# Revit family: RN 55046 Optipress-Therm-Vis de rappel
name_source: partatom
category: Rohrformteile
units: mm (PartAtom-declared; Revit-internal decimal feet)

## family parameters
Arbeitsebenenbasiert = Nein
Beim Laden mit Abzugskörper schneiden = Nein
Bemaßung runder Anschluss = Durchmesser verwenden
Gemeinsam genutzt = Nein
Immer vertikal = Ja
Teiletyp = Verbindung

## types (7) — shared parameters
1.010.00.2 Blattnummer der Richtlinie = 29
1.010.00.3 Ausgabedatum (Monat) der Richtlinie = 201308
1.010.00.4 Herstellername = R. Nussbaum AG
1.010.00.5 Revisionsdatum der Datei = 20190521
1.010.00.6 Webadresse des Herstellers = http://www.nussbaum.ch
1.100.00.4 Produktbezeichnung = Versorgung
1.110.00.2 Index = 1
1.110.00.4 Produktbezeichnung = Optipress-Therm
1.960/3L.00.8 Link (URL) = https://www.nussbaum.ch
29.700.00.4 Produktname = Optipress-Therm-Verschraubung, mit Aussengewinde
29.700.00.5 Produktkennung = 2
29.700.00.6 Querschnittsform = 1
29.700.00.7 Nennweitensystem = DN
29.700.00.8 Nenndrucksystem = PN
29.710.02.4 Nenndruck = 16
29.710.02.5 max. zul. Überdruck [hPa] = 1600
29.710.02.7 max. zul. Dauer-Betriebsdruck [hPa] = 1600
29.710.02.9 max. zul. Dauer-Betriebstemperatur [°C] = 95
Connector Visibility = Nein
EnclosingSpace Visibility = Nein
Hersteller = R. Nussbaum AG

## per-type parameters (varying)
| type | 1.800.00.3 TGA-Nummer | 1.800.00.4 Kommentarfeld | 1.810.00.3 Hersteller-Bestellnummer | 1.810.00.4 DATANORM-Nummer | 1.810.00.5 StLB-Nummer | 1.810.00.6 GTIN-Nummer | 29.710.02.10 Formstück-Gewicht [kg] | 29.710.02.3 Benennung | CONNECTOR0_DIAMETER_dX_0r | CONNECTOR0_dX_01 | CONNECTOR0_ref_dX | CONNECTOR1_DIAMETER_dX_0r | CONNECTOR1_dX_00 | CONNECTOR1_dX_01 | CONNECTOR1_ref_dX | Modell | R. Nussbaum AG 55046.22 de Visibility | R. Nussbaum AG 55046.25 de Visibility | R. Nussbaum AG 55046.26 de Visibility | R. Nussbaum AG 55046.27 de Visibility | R. Nussbaum AG 55046.28 de Visibility | R. Nussbaum AG 55046.29 de Visibility | R. Nussbaum AG 55046.30 de Visibility | Typenkommentare |
| DN=1 | 01900100000000000000000000000000000000000000000026000000000000000007 | 55046.30, Optipress-Therm-Verschraubung, mit Aussengewinde, DN=20, L=76, R=1 | 55046.3 | 55046.30 | 256.114 | 7612945685841 | 0.227 | Optipress-Therm-Verschraubung, mit Aussengewinde, DN=20, L=76, R=1 | 20 mm | 24 mm  [stored 0.0787402 ft] | 24 mm  [stored 0.0787402 ft] | 25 mm  [stored 0.082021 ft] | 59 mm | 76 mm | 59 mm | 55046.3 | Nein | Nein | Nein | Nein | Nein | Nein | Ja | Optipress-Therm-Vis de rappel DN=20 |
| DN=50 | 01900100000000000000000000000000000000000000000026000000000000000006 | 55046.29, Optipress-Therm-Verschraubung, mit Aussengewinde, DN=50, L=109, R=2 | 55046.29 | 55046.29 | 256.168 | 7612945663757 | 1.059 | Optipress-Therm-Verschraubung, mit Aussengewinde, DN=50, L=109, R=2 | 50 mm | 40 mm | 40 mm | 50 mm | 85 mm | 109 mm  [stored 0.357612 ft] | 85 mm | 55046.29 | Nein | Nein | Nein | Nein | Nein | Ja | Nein | Optipress-Therm-Vis de rappel DN=50 |
| DN=40 | 01900100000000000000000000000000000000000000000026000000000000000005 | 55046.28, Optipress-Therm-Verschraubung, mit Aussengewinde, DN=40, L=95, R=1½ | 55046.28 | 55046.28 | 256.157 | 7612945663740 | 0.564 | Optipress-Therm-Verschraubung, mit Aussengewinde, DN=40, L=95, R=1½ | 40 mm | 36 mm | 36 mm | 40 mm | 76 mm | 95 mm | 76 mm | 55046.28 | Nein | Nein | Nein | Nein | Ja | Nein | Nein | Optipress-Therm-Vis de rappel DN=40 |
| DN=32 | 01900100000000000000000000000000000000000000000026000000000000000004 | 55046.27, Optipress-Therm-Verschraubung, mit Aussengewinde, DN=32, L=83, R=1¼ | 55046.27 | 55046.27 | 256.146 | 7612945663733 | 0.417 | Optipress-Therm-Verschraubung, mit Aussengewinde, DN=32, L=83, R=1¼ | 32 mm  [stored 0.104987 ft] | 26 mm | 26 mm | 32 mm  [stored 0.104987 ft] | 65 mm | 84 mm | 65 mm | 55046.27 | Nein | Nein | Nein | Ja | Nein | Nein | Nein | Optipress-Therm-Vis de rappel DN=32 |
| DN=25 | 01900100000000000000000000000000000000000000000026000000000000000003 | 55046.26, Optipress-Therm-Verschraubung, mit Aussengewinde, DN=25, L=87, R=1 | 55046.26 | 55046.26 | 256.135 | 7612945663719 | 0.25 | Optipress-Therm-Verschraubung, mit Aussengewinde, DN=25, L=87, R=1 | 25 mm  [stored 0.082021 ft] | 24 mm  [stored 0.0787402 ft] | 24 mm  [stored 0.0787402 ft] | 25 mm  [stored 0.082021 ft] | 70 mm | 87 mm | 70 mm | 55046.26 | Nein | Nein | Ja | Nein | Nein | Nein | Nein | Optipress-Therm-Vis de rappel DN=25 |
| DN=20 | 01900100000000000000000000000000000000000000000026000000000000000002 | 55046.25, Optipress-Therm-Verschraubung, mit Aussengewinde, DN=20, L=77, R=¾ | 55046.25 | 55046.25 | 256.124 | 7612945663689 | 0.148 | Optipress-Therm-Verschraubung, mit Aussengewinde, DN=20, L=77, R=¾ | 20 mm | 24 mm  [stored 0.0787402 ft] | 24 mm  [stored 0.0787402 ft] | 20 mm | 62 mm | 77 mm | 62 mm | 55046.25 | Nein | Ja | Nein | Nein | Nein | Nein | Nein | Optipress-Therm-Vis de rappel DN=20 |
| DN=12x15 | 01900100000000000000000000000000000000000000000026000000000000000001 | 55046.22, Optipress-Therm-Verschraubung, mit Aussengewinde, DN=12x15, L=67, R=½ | 55046.22 | 55046.22 | 256.112 | 7612945663672 | 0.127 | Optipress-Therm-Verschraubung, mit Aussengewinde, DN=12x15, L=67, R=½ | 12 mm  [stored 0.0393701 ft] | 22 mm | 22 mm | 15 mm  [stored 0.0492126 ft] | 54 mm | 67 mm | 54 mm | 55046.22 | Ja | Nein | Nein | Nein | Nein | Nein | Nein | Optipress-Therm-Vis de rappel DN=12x15 |

note: [stored X ft] marks values corroborated as IEEE doubles in the binary element streams (Revit-internal decimal feet)
